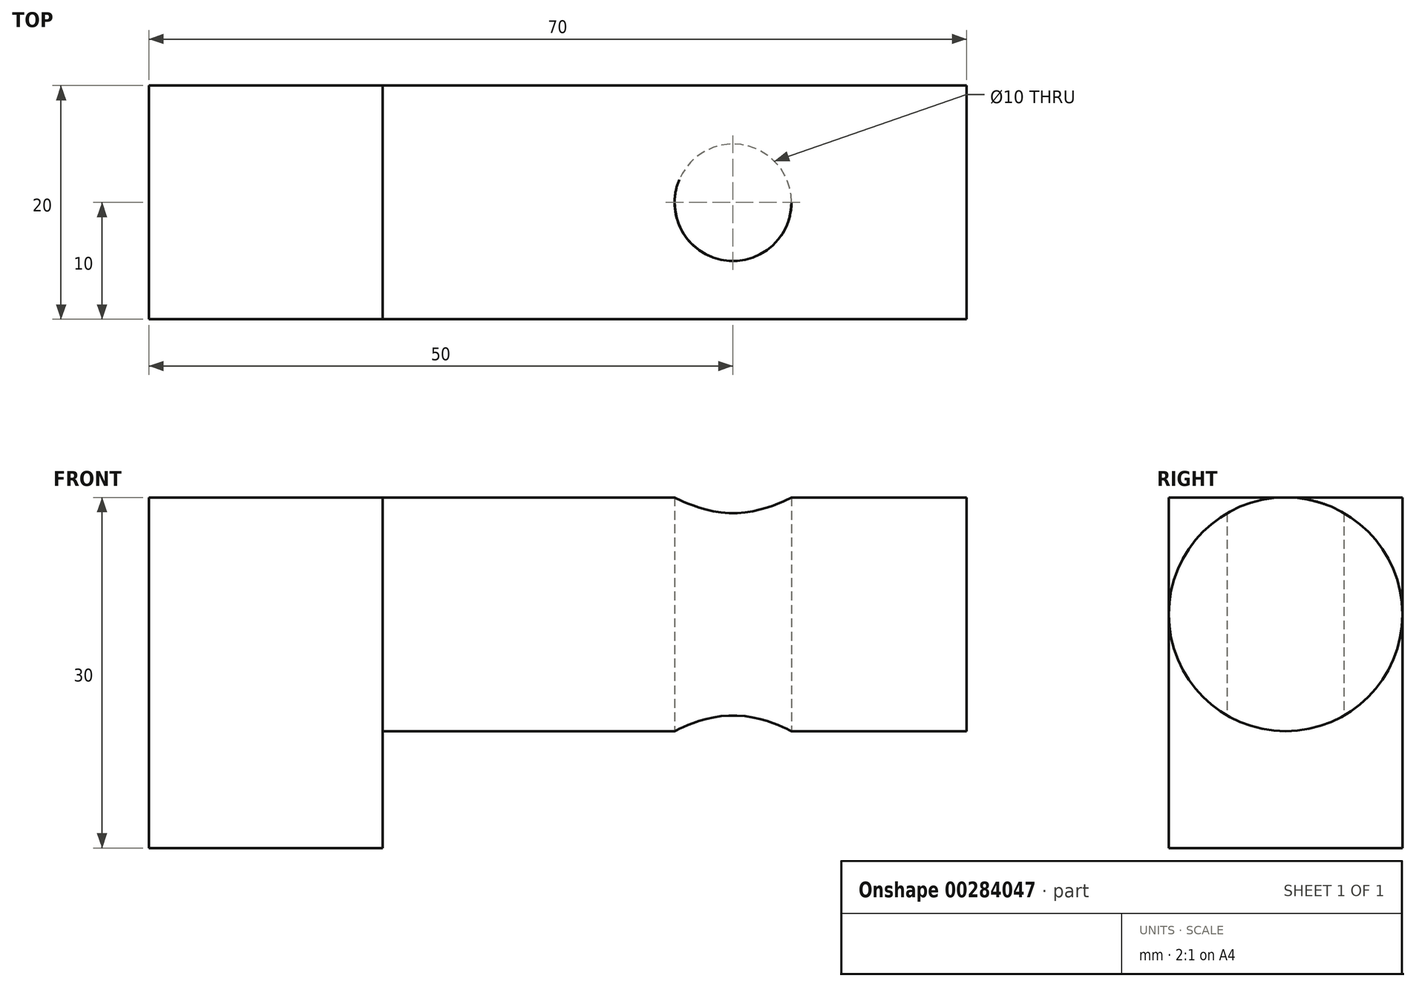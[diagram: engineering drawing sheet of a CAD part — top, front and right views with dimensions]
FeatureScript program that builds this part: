
annotation { "Feature Type Name" : "Feature", "Feature Type Description" : "" }
export const myFeature = defineFeature(function(context is Context, id is Id, definition is map)
    precondition{}
    {
        {
            var Q0;
            Q0=qCreatedBy(makeId("Front.planeOp"),FACE);
            var sketch = newSketch(context, id + "F0", { "sketchPlane" : qUnion([Q0])});
            skLineSegment(sketch, "E0.bottom", {"start": v(10, -15) * mm, "end": v(-10, -15) * mm});
            skLineSegment(sketch, "E0.top", {"start": v(10, 15) * mm, "end": v(-10, 15) * mm});
            skLineSegment(sketch, "E0.left", {"start": v(10, -15) * mm, "end": v(10, 15) * mm});
            skLineSegment(sketch, "E0.right", {"start": v(-10, -15) * mm, "end": v(-10, 15) * mm});
            skPoint(sketch, "E0.middle", {"position": v(0, 0) * mm});
            skSolve(sketch);
        }
        {
            var Q0;
            Q0 = qSketchRegion(id + "F0", true);
            extrude(context, id + "F1", {"entities" : qUnion([Q0]), "depth" : 20 * mm});
        }
        {
            var Q0;
            Q0=makeQuery(id+"F1.opExtrude","SWEPT_FACE",FACE,{"disambiguationData":[OSD([sQuery(id+"F0.wireOp",EDGE,"E0.left")])]});
            var sketch = newSketch(context, id + "F2", { "sketchPlane" : qUnion([Q0])});
            skCircle(sketch, "E1", {"center": v(-10, 5) * mm, "radius": 10 * mm});
            skSolve(sketch);
        }
        {
            var Q0;
            Q0 = qSketchRegion(id + "F2", true);
            extrude(context, id + "F3", {"entities" : qUnion([Q0]), "operationType" : NewBodyOperationType.ADD, "depth" : 50 * mm});
        }
        {
            var Q0;
            Q0=makeQuery(id+"F1.opExtrude","SWEPT_FACE",FACE,{"disambiguationData":[OSD([sQuery(id+"F0.wireOp",EDGE,"E0.bottom")])]});
            var sketch = newSketch(context, id + "F4", { "sketchPlane" : qUnion([Q0])});
            skCircle(sketch, "E2", {"center": v(40, 10) * mm, "radius": 5 * mm});
            skPoint(sketch, "E2.centerSnap0", {"position": v(10, 10) * mm});
            skSolve(sketch);
        }
        {
            var Q0;
            Q0=makeQuery(id+"F4.imprint","IMPRINT",FACE,{"disambiguationData":[TD([[makeQuery(id+"F4.imprint","IMPRINT",EDGE,{"derivedFrom":sQuery(id+"F4.wireOp",EDGE,"E2")}),1.0]])]});
            extrude(context, id + "F5", {"entities" : qUnion([Q0]), "operationType" : NewBodyOperationType.REMOVE, "endBound" : BoundingType.THROUGH_ALL, "oppositeDirection" : true, "depth" : 40.8 * mm});
        }
    });
